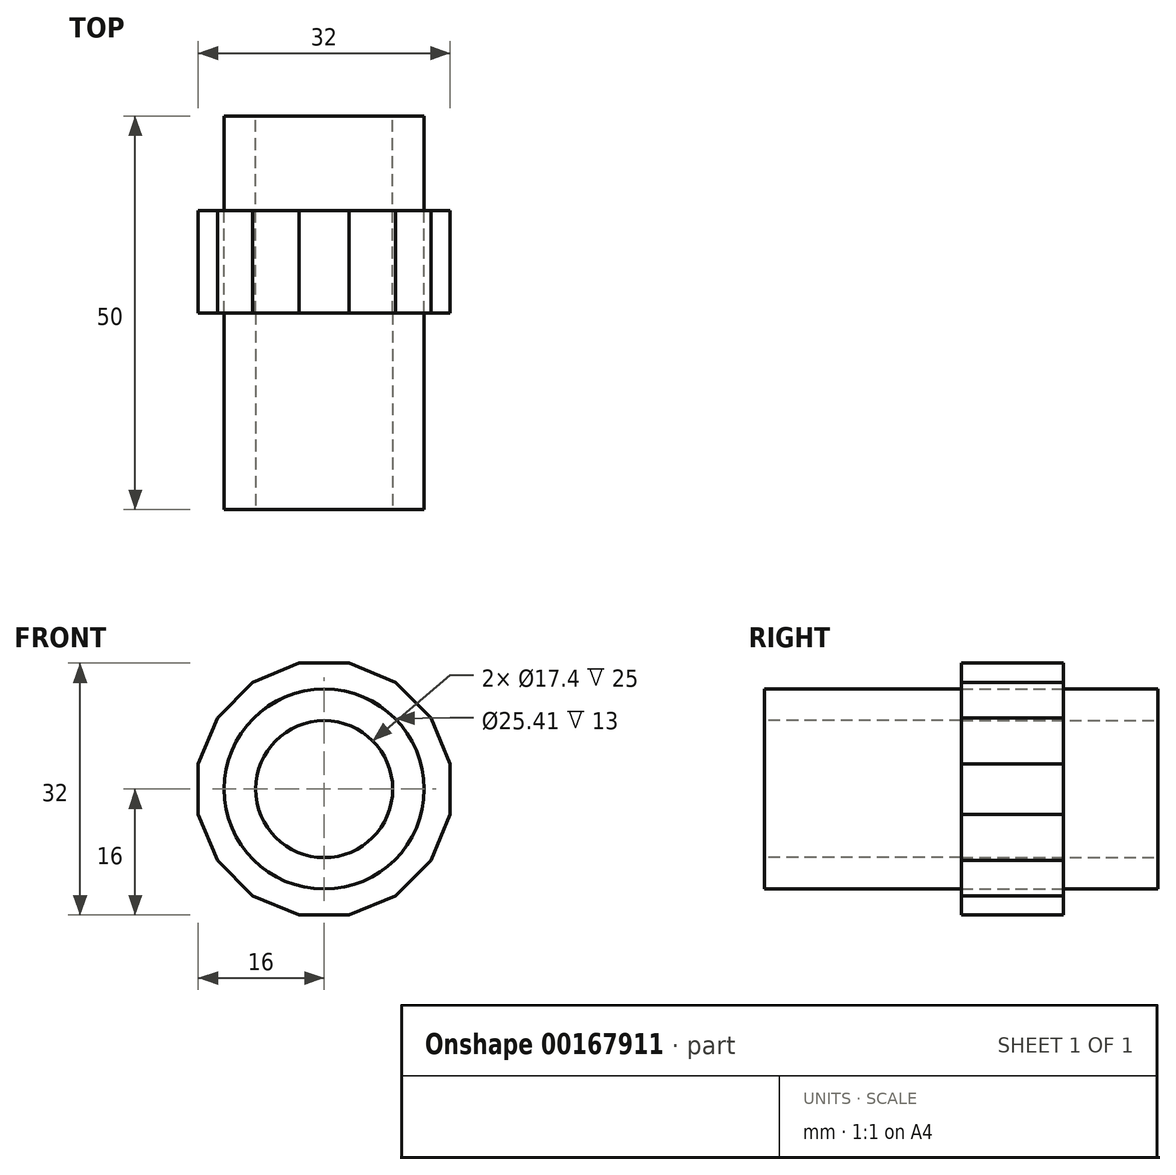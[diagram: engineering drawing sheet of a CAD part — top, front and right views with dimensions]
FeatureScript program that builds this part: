
annotation { "Feature Type Name" : "Feature", "Feature Type Description" : "" }
export const myFeature = defineFeature(function(context is Context, id is Id, definition is map)
    precondition{}
    {
        {
            var Q0;
            Q0=qCreatedBy(makeId("Front.planeOp"),FACE);
            var sketch = newSketch(context, id + "F0", { "sketchPlane" : qUnion([Q0])});
            skCircle(sketch, "E0.cCircle", {"center": v(0, 0) * mm, "radius": 16 * mm, "construction": true});
            skLineSegment(sketch, "E0.0", {"start": v(-16, -3.18) * mm, "end": v(-16, 3.18) * mm});
            skLineSegment(sketch, "E0.1", {"start": v(-16, 3.18) * mm, "end": v(-13.56, 9.06) * mm});
            skLineSegment(sketch, "E0.2", {"start": v(-13.56, 9.06) * mm, "end": v(-9.06, 13.56) * mm});
            skLineSegment(sketch, "E0.3", {"start": v(-9.06, 13.56) * mm, "end": v(-3.18, 16) * mm});
            skLineSegment(sketch, "E0.4", {"start": v(-3.18, 16) * mm, "end": v(3.18, 16) * mm});
            skLineSegment(sketch, "E0.5", {"start": v(3.18, 16) * mm, "end": v(9.06, 13.56) * mm});
            skLineSegment(sketch, "E0.6", {"start": v(9.06, 13.56) * mm, "end": v(13.56, 9.06) * mm});
            skLineSegment(sketch, "E0.7", {"start": v(13.56, 9.06) * mm, "end": v(16, 3.18) * mm});
            skLineSegment(sketch, "E0.8", {"start": v(16, 3.18) * mm, "end": v(16, -3.18) * mm});
            skLineSegment(sketch, "E0.9", {"start": v(16, -3.18) * mm, "end": v(13.56, -9.06) * mm});
            skLineSegment(sketch, "E0.10", {"start": v(13.56, -9.06) * mm, "end": v(9.06, -13.56) * mm});
            skLineSegment(sketch, "E0.11", {"start": v(9.06, -13.56) * mm, "end": v(3.18, -16) * mm});
            skLineSegment(sketch, "E0.12", {"start": v(3.18, -16) * mm, "end": v(-3.18, -16) * mm});
            skLineSegment(sketch, "E0.13", {"start": v(-3.18, -16) * mm, "end": v(-9.06, -13.56) * mm});
            skLineSegment(sketch, "E0.14", {"start": v(-9.06, -13.56) * mm, "end": v(-13.56, -9.06) * mm});
            skLineSegment(sketch, "E0.15", {"start": v(-13.56, -9.06) * mm, "end": v(-16, -3.18) * mm});
            skPoint(sketch, "E0.0.midPoint", {"position": v(-16, 0) * mm});
            skCircle(sketch, "E1", {"center": v(0, 0) * mm, "radius": 12.7 * mm});
            skCircle(sketch, "E2", {"center": v(0, 0) * mm, "radius": 8.7 * mm});
            skSolve(sketch);
        }
        {
            var Q0;
            Q0=makeQuery(id+"F0.imprint","IMPRINT",FACE,{"disambiguationData":[TD([[makeQuery(id+"F0.imprint","IMPRINT",EDGE,{"derivedFrom":sQuery(id+"F0.wireOp",EDGE,"E1")}),1.0]])]});
            extrude(context, id + "F1", {"entities" : qUnion([Q0]), "depth" : 13 * mm});
        }
        {
            var Q0;
            Q0=makeQuery(id+"F0.imprint","IMPRINT",FACE,{"disambiguationData":[TD([[makeQuery(id+"F0.imprint","IMPRINT",EDGE,{"derivedFrom":sQuery(id+"F0.wireOp",EDGE,"E1")}),1.0]])]});
            extrude(context, id + "F2", {"entities" : qUnion([Q0]), "operationType" : NewBodyOperationType.ADD, "oppositeDirection" : true, "depth" : 12 * mm});
        }
        {
            var Q0;
            Q0=makeQuery(id+"F0.imprint","IMPRINT",FACE,{"disambiguationData":[TD([[makeQuery(id+"F0.imprint","IMPRINT",EDGE,{"derivedFrom":sQuery(id+"F0.wireOp",EDGE,"E0.0")}),-1.0]])]});
            extrude(context, id + "F3", {"entities" : qUnion([Q0]), "operationType" : NewBodyOperationType.ADD, "depth" : 13 * mm});
        }
        {
            var Q0;
            Q0=makeQuery(id+"F1.opExtrude","SWEPT_BODY",BODY,{"disambiguationData":[OSD([sQuery(id+"F0.wireOp",EDGE,"E1"),sQuery(id+"F0.wireOp",EDGE,"E1")])]});
            var Q1;
            {var subQ0=sQuery(id+"F0.wireOp",EDGE,"E1");Q1=makeQuery(id+"F3.boolean.opBoolean","MERGE",FACE,{"derivedFrom":[makeQuery(id+"F1.opExtrude","CAP_FACE",FACE,{"disambiguationData":[OSD([subQ0,sQuery(id+"F0.wireOp",EDGE,"E1")])],"isStart":false}),makeQuery(id+"F3.opExtrude","CAP_FACE",FACE,{"disambiguationData":[OSD([sQuery(id+"F0.wireOp",EDGE,"E0.0"),sQuery(id+"F0.wireOp",EDGE,"E0.1"),sQuery(id+"F0.wireOp",EDGE,"E0.2"),sQuery(id+"F0.wireOp",EDGE,"E0.3"),sQuery(id+"F0.wireOp",EDGE,"E0.4"),sQuery(id+"F0.wireOp",EDGE,"E0.5"),sQuery(id+"F0.wireOp",EDGE,"E0.6"),sQuery(id+"F0.wireOp",EDGE,"E0.7"),sQuery(id+"F0.wireOp",EDGE,"E0.8"),sQuery(id+"F0.wireOp",EDGE,"E0.9"),sQuery(id+"F0.wireOp",EDGE,"E0.10"),sQuery(id+"F0.wireOp",EDGE,"E0.11"),sQuery(id+"F0.wireOp",EDGE,"E0.12"),sQuery(id+"F0.wireOp",EDGE,"E0.13"),sQuery(id+"F0.wireOp",EDGE,"E0.14"),sQuery(id+"F0.wireOp",EDGE,"E0.15"),subQ0])],"isStart":false})]});}
            mirror(context, id + "F4", {"operationType" : NewBodyOperationType.ADD, "entities" : qUnion([Q0]), "mirrorPlane" : qUnion([Q1])});
        }
    });
